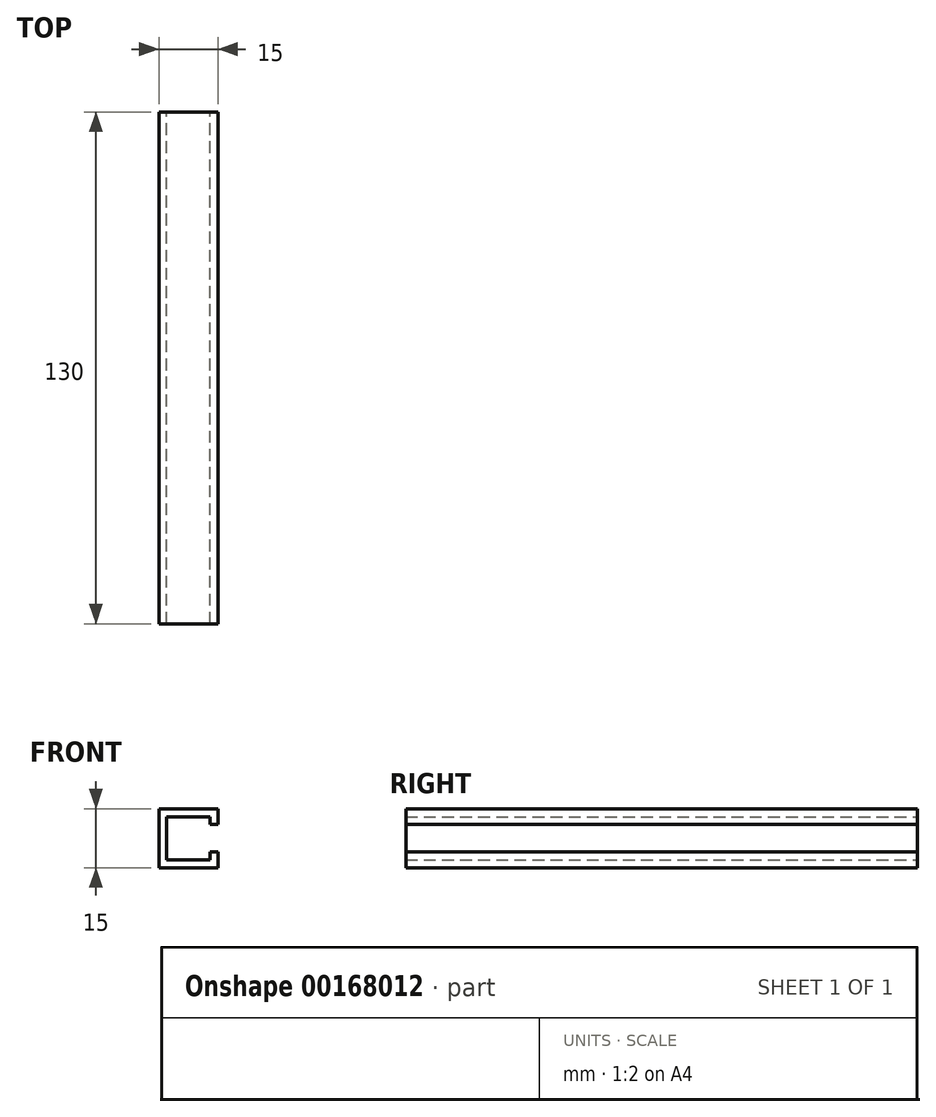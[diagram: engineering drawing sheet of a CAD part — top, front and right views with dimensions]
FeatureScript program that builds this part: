
annotation { "Feature Type Name" : "Feature", "Feature Type Description" : "" }
export const myFeature = defineFeature(function(context is Context, id is Id, definition is map)
    precondition{}
    {
        {
            var Q0;
            Q0=qCreatedBy(makeId("Front.planeOp"),FACE);
            var sketch = newSketch(context, id + "F0", { "sketchPlane" : qUnion([Q0])});
            skLineSegment(sketch, "E0.bottom", {"start": v(7.5, 7.5) * mm, "end": v(-7.5, 7.5) * mm});
            skLineSegment(sketch, "E0.top", {"start": v(7.5, -7.5) * mm, "end": v(-7.5, -7.5) * mm});
            skLineSegment(sketch, "E0.right", {"start": v(-7.5, 7.5) * mm, "end": v(-7.5, -7.5) * mm});
            skPoint(sketch, "E0.middle", {"position": v(0, 0) * mm});
            skLineSegment(sketch, "E1.0", {"start": v(5.5, -5.5) * mm, "end": v(-5.5, -5.5) * mm});
            skLineSegment(sketch, "E1.1", {"start": v(-5.5, 5.5) * mm, "end": v(-5.5, -5.5) * mm});
            skLineSegment(sketch, "E1.2", {"start": v(5.5, 5.5) * mm, "end": v(-5.5, 5.5) * mm});
            skLineSegment(sketch, "E2", {"start": v(7.5, 3.5) * mm, "end": v(5.5, 3.5) * mm});
            skLineSegment(sketch, "E3", {"start": v(5.5, 3.5) * mm, "end": v(5.5, 5.5) * mm});
            skLineSegment(sketch, "E4", {"start": v(7.5, 3.5) * mm, "end": v(7.5, 7.5) * mm});
            skLineSegment(sketch, "E5.MirrorCS", {"start": v(5.5, -3.5) * mm, "end": v(5.5, -5.5) * mm});
            skLineSegment(sketch, "E6.MirrorCS", {"start": v(7.5, -3.5) * mm, "end": v(7.5, -7.5) * mm});
            skLineSegment(sketch, "E7.MirrorCS", {"start": v(7.5, -3.5) * mm, "end": v(5.5, -3.5) * mm});
            skSolve(sketch);
        }
        {
            var Q0;
            Q0 = qSketchRegion(id + "F0", true);
            extrude(context, id + "F1", {"entities" : qUnion([Q0]), "depth" : 130 * mm, "symmetric" : true});
        }
    });
